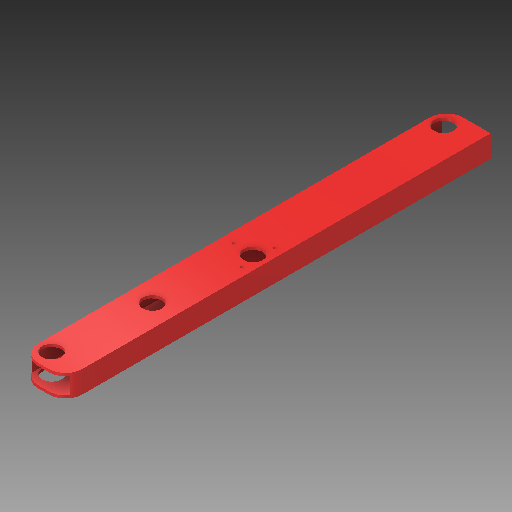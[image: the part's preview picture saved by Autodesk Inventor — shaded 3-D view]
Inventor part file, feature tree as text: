
AUTODESK INVENTOR PART (.ipt)
format: ipt  version: 2017 SP1 (Build 210196100, 196)  size: 157,184 bytes
history: native  units: in
note: dims shown in document units (in); Inventor stores cm internally (conversion verified against a paired STEP export)
features: extrude x2, sketch x2, fillet x1
ambient origin geometry x8: Origin, YZ Plane, XZ Plane, XY Plane, X Axis, Y Axis, Z Axis, Center Point
bodies: Solid1 (feature_tree)
feature tree (5):
  extrude  "Extrusion1"  Depth=2.0in
  extrude  "Extrusion2"  Depth=19.25in TaperAngle=0.0deg
  fillet  "Fillet1"  Radius=0.875in
  sketch  "Sketch1"  dims[d0=1.0in d1=2.0in]
  sketch  "Sketch2"  dims[d2=0.125in d3=19.25in d4=0.0in d5=0.875in d10=0.875in d11=20.0in d12=0.0in d13=0.75in d16=0.75in d17=0.625in d20=0.75in d21=0.625in d23=0.625in d24=1.5in d27=1.125in d28=0.15in d29=0.875in d30=0.375in d31=4.201in]
